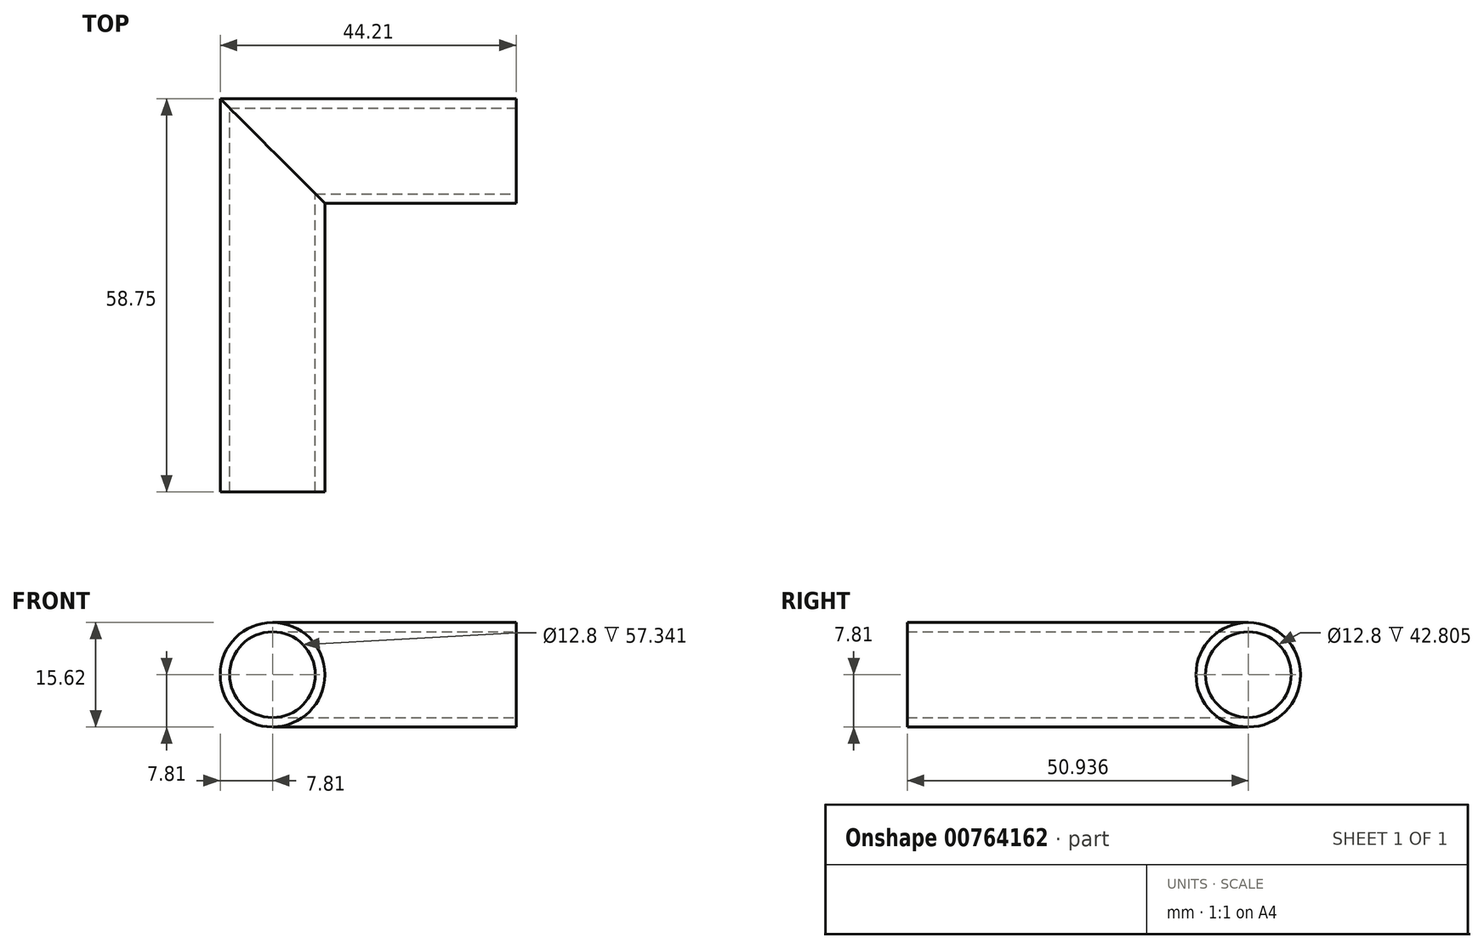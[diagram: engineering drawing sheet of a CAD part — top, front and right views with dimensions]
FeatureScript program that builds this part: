
annotation { "Feature Type Name" : "Feature", "Feature Type Description" : "" }
export const myFeature = defineFeature(function(context is Context, id is Id, definition is map)
    precondition{}
    {
        {
            var Q0;
            Q0=qCreatedBy(makeId("Top.planeOp"),FACE);
            var sketch = newSketch(context, id + "F0", { "sketchPlane" : qUnion([Q0])});
            skLineSegment(sketch, "E0", {"start": v(0, 0) * mm, "end": v(0, 50.94) * mm});
            skLineSegment(sketch, "E1", {"start": v(0, 50.94) * mm, "end": v(36.4, 50.94) * mm});
            skSolve(sketch);
        }
        {
            var Q0;
            Q0=qCreatedBy(makeId("Front.planeOp"),FACE);
            var sketch = newSketch(context, id + "F1", { "sketchPlane" : qUnion([Q0])});
            skCircle(sketch, "E2", {"center": v(0, 0) * mm, "radius": 6.4 * mm});
            skCircle(sketch, "E3", {"center": v(0, 0) * mm, "radius": 7.81 * mm});
            skSolve(sketch);
        }
        {
            var Q0;
            Q0=makeQuery(id+"F1.imprint","IMPRINT",FACE,{"disambiguationData":[TD([[makeQuery(id+"F1.imprint","IMPRINT",EDGE,{"derivedFrom":sQuery(id+"F1.wireOp",EDGE,"E2")}),-1.0]])]});
            var Q1;
            Q1=sQuery(id+"F0.wireOp",EDGE,"E0");
            var Q2;
            Q2=sQuery(id+"F0.wireOp",EDGE,"E1");
            sweep(context, id + "F2", {"profiles" : qUnion([Q0]), "path" : qUnion([Q1, Q2])});
        }
    });
